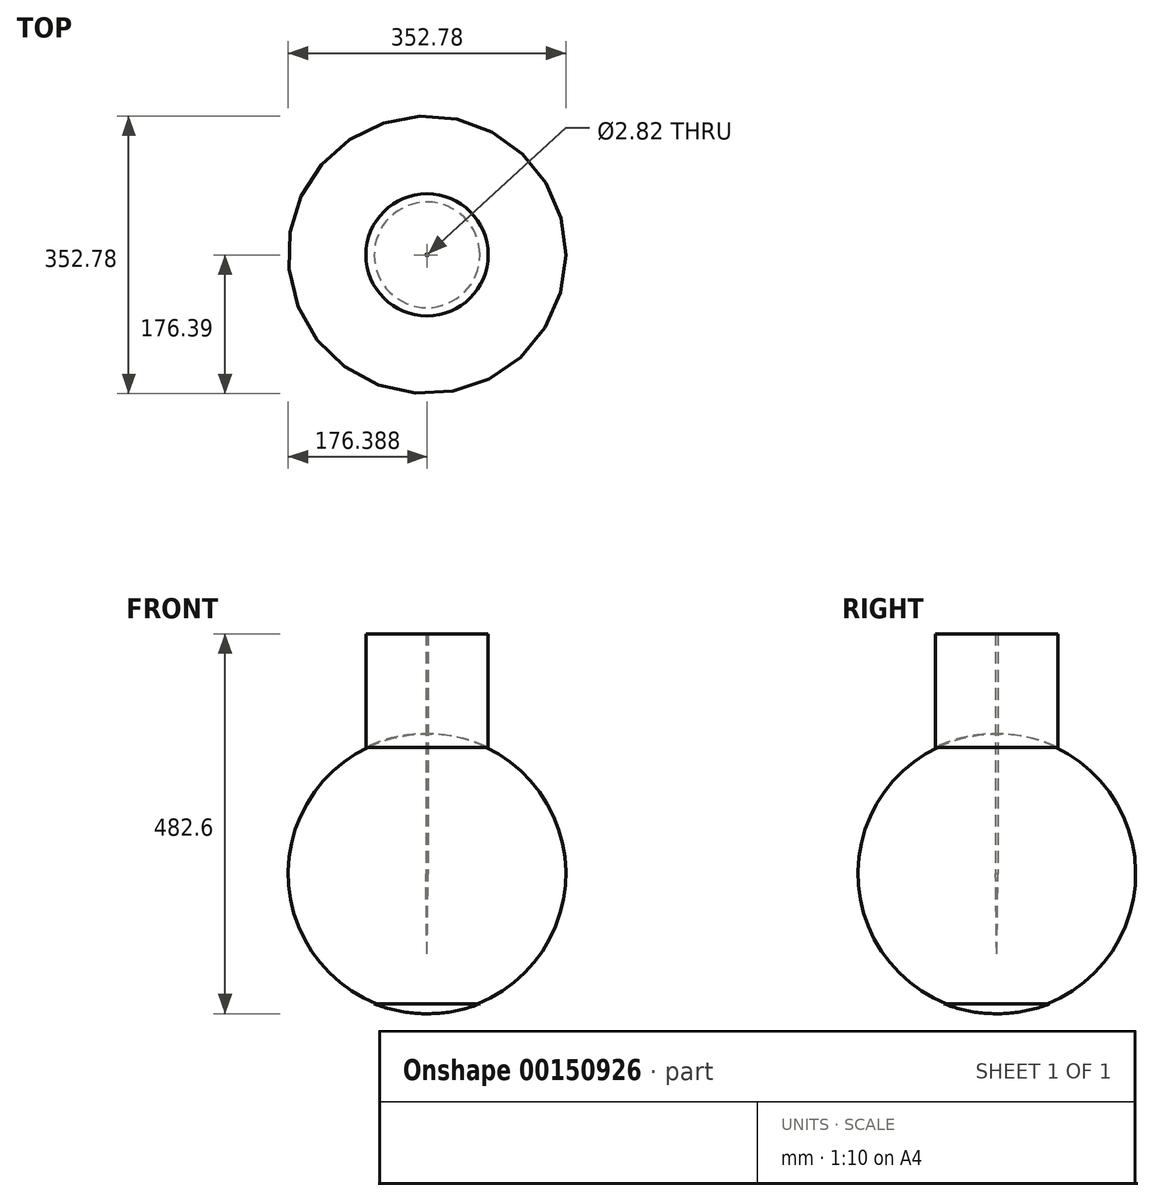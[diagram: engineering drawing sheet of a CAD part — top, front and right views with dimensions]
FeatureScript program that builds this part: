
annotation { "Feature Type Name" : "Feature", "Feature Type Description" : "" }
export const myFeature = defineFeature(function(context is Context, id is Id, definition is map)
    precondition{}
    {
        {
            var Q0;
            Q0=qCreatedBy(makeId("Front.planeOp"),FACE);
            var sketch = newSketch(context, id + "F0", { "sketchPlane" : qUnion([Q0])});
            skLineSegment(sketch, "E0", {"start": v(0, 0) * mm, "end": v(-177.8, 0) * mm});
            skLineSegment(sketch, "E1", {"start": v(1.4, -101.6) * mm, "end": v(-145.91, -101.6) * mm});
            skArc(sketch, "E2", {"start": v(0, 177.8) * mm, "mid": v(-67.2, 164.61) * mm, "end": v(-124.43, 127) * mm});
            skLineSegment(sketch, "E3", {"start": v(-124.43, 127) * mm, "end": v(-124.43, 127) * mm});
            skArc(sketch, "E4", {"start": v(-124.43, 127) * mm, "mid": v(-177.02, 16.63) * mm, "end": v(-145.91, -101.6) * mm});
            skLineSegment(sketch, "E5", {"start": v(-124.43, 127) * mm, "end": v(0, 127) * mm});
            skArc(sketch, "E6", {"start": v(-145.91, -101.6) * mm, "mid": v(-110.47, -139.32) * mm, "end": v(-65.66, -165.23) * mm});
            skLineSegment(sketch, "E7", {"start": v(-145.91, -101.6) * mm, "end": v(-145.91, -101.6) * mm});
            skLineSegment(sketch, "E8.trimOffspring", {"start": v(0, 0) * mm, "end": v(0, 127) * mm});
            skLineSegment(sketch, "E9", {"start": v(0, 0) * mm, "end": v(1.4, -101.6) * mm});
            skLineSegment(sketch, "E10", {"start": v(-65.66, -165.23) * mm, "end": v(-65.66, -165.23) * mm});
            skLineSegment(sketch, "E11", {"start": v(1.4, -165.1) * mm, "end": v(1.4, -101.6) * mm});
            skLineSegment(sketch, "E12", {"start": v(1.4, -165.1) * mm, "end": v(-65.66, -165.23) * mm});
            skLineSegment(sketch, "E13", {"start": v(-76.2, 304.8) * mm, "end": v(-76.2, 160.64) * mm});
            skLineSegment(sketch, "E14", {"start": v(0, 127) * mm, "end": v(0, 177.8) * mm});
            skLineSegment(sketch, "E15", {"start": v(0, 177.8) * mm, "end": v(0, 304.8) * mm});
            skLineSegment(sketch, "E16", {"start": v(-76.2, 304.8) * mm, "end": v(0, 304.8) * mm});
            skSolve(sketch);
        }
        {
            var Q0;
            {var subQ0=sQuery(id+"F0.wireOp",EDGE,"E5");Q0=makeQuery(id+"F0.imprint","IMPRINT",FACE,{"disambiguationData":[TD([[makeQuery(id+"F0.imprint","IMPRINT",EDGE,{"derivedFrom":subQ0}),1.0]])]});}
            var Q1;
            {var subQ0=sQuery(id+"F0.wireOp",EDGE,"E0");Q1=makeQuery(id+"F0.imprint","IMPRINT",FACE,{"disambiguationData":[TD([[makeQuery(id+"F0.imprint","IMPRINT",EDGE,{"derivedFrom":subQ0}),-1.0]])]});}
            var Q2;
            {var subQ0=sQuery(id+"F0.wireOp",EDGE,"E0");Q2=makeQuery(id+"F0.imprint","IMPRINT",FACE,{"disambiguationData":[TD([[makeQuery(id+"F0.imprint","IMPRINT",EDGE,{"derivedFrom":subQ0}),1.0]])]});}
            var Q3;
            Q3=makeQuery(id+"F0.imprint","IMPRINT",FACE,{"disambiguationData":[TD([[makeQuery(id+"F0.imprint","IMPRINT",EDGE,{"derivedFrom":sQuery(id+"F0.wireOp",EDGE,"E1")}),1.0]])]});
            var Q4;
            {var subQ0=sQuery(id+"F0.wireOp",EDGE,"qsQoIZYw-8uiN-iF2j-CMVE-Z6aCpoR0AQx2");Q4=makeQuery(id+"F0.imprint","IMPRINT",FACE,{"disambiguationData":[TD([[makeQuery(id+"F0.imprint","IMPRINT",EDGE,{"derivedFrom":subQ0}),1.0]])]});}
            var Q5;
            {var subQ2=sQuery(id+"F0.wireOp",EDGE,"E13");Q5=makeQuery(id+"F0.imprint","IMPRINT",FACE,{"disambiguationData":[TD([[makeQuery(id+"F0.imprint","IMPRINT",EDGE,{"derivedFrom":subQ2}),1.0]])]});}
            var Q6;
            Q6=sQuery(id+"F0.wireOp",EDGE,"E11");
            revolve(context, id + "F1", {"entities" : qUnion([Q0, Q1, Q2, Q3, Q4, Q5]), "axis" : qUnion([Q6]), "revolveType" : RevolveType.FULL});
        }
    });
